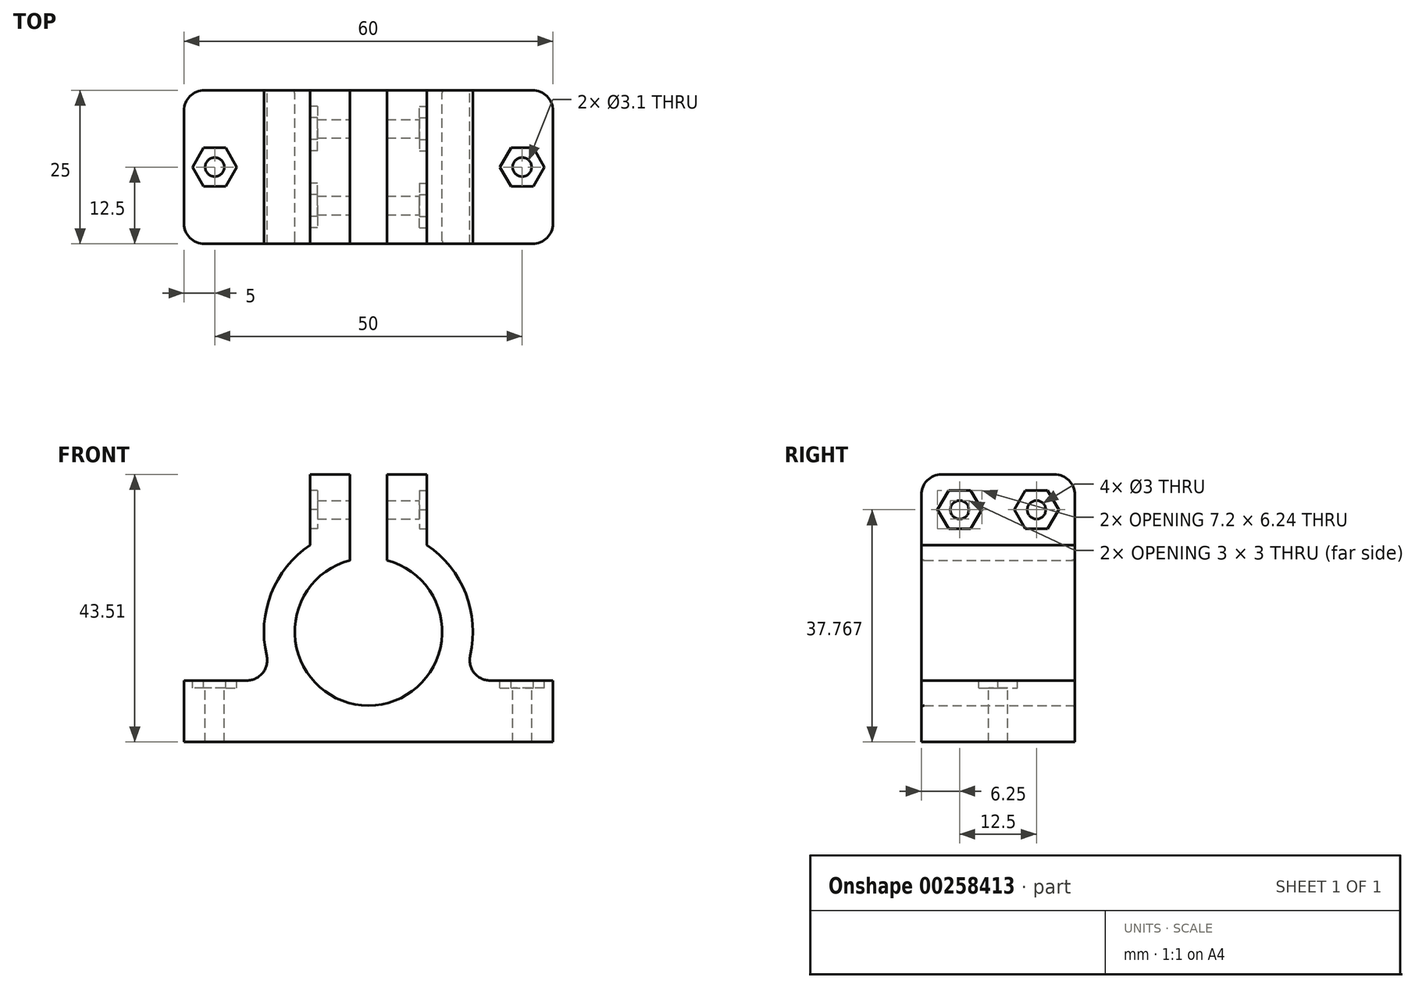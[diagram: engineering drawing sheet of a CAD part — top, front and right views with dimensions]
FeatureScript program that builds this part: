
annotation { "Feature Type Name" : "Feature", "Feature Type Description" : "" }
export const myFeature = defineFeature(function(context is Context, id is Id, definition is map)
    precondition{}
    {
        {
            var Q0;
            Q0=qCreatedBy(makeId("Front.planeOp"),FACE);
            var sketch = newSketch(context, id + "F0", { "sketchPlane" : qUnion([Q0])});
            skLineSegment(sketch, "E0.bottom", {"start": v(30, -29.77) * mm, "end": v(-30, -29.77) * mm});
            skLineSegment(sketch, "E0.left", {"start": v(30, -29.77) * mm, "end": v(30, -19.77) * mm});
            skLineSegment(sketch, "E0.right", {"start": v(-30, -29.77) * mm, "end": v(-30, -19.77) * mm});
            skPoint(sketch, "E0.middle", {"position": v(0, -24.77) * mm});
            skLineSegment(sketch, "E1", {"start": v(0, -29.77) * mm, "end": v(0, 6.08) * mm, "construction": true});
            skArc(sketch, "E2", {"start": v(-3, -0.23) * mm, "mid": v(0, -23.85) * mm, "end": v(3, -0.23) * mm});
            skArc(sketch, "E3.0", {"start": v(15.04, -19.77) * mm, "mid": v(16.49, -7.7) * mm, "end": v(9.5, 2.25) * mm});
            skLineSegment(sketch, "E4", {"start": v(-30, -19.77) * mm, "end": v(-15.04, -19.77) * mm});
            skLineSegment(sketch, "E5.MirrorCS", {"start": v(30, -19.77) * mm, "end": v(15.04, -19.77) * mm});
            skLineSegment(sketch, "E6.top", {"start": v(-9.5, 13.74) * mm, "end": v(-3, 13.74) * mm});
            skLineSegment(sketch, "E6.left", {"start": v(-9.5, 2.25) * mm, "end": v(-9.5, 13.74) * mm});
            skLineSegment(sketch, "E6.right", {"start": v(-3, 4.89) * mm, "end": v(-3, 13.74) * mm});
            skLineSegment(sketch, "E7.MirrorCS", {"start": v(3, 4.89) * mm, "end": v(3, 13.74) * mm});
            skLineSegment(sketch, "E8.MirrorCS", {"start": v(9.5, 2.25) * mm, "end": v(9.5, 13.74) * mm});
            skLineSegment(sketch, "E9.MirrorCS", {"start": v(9.5, 13.74) * mm, "end": v(3, 13.74) * mm});
            skArc(sketch, "E10.trimOffspring", {"start": v(-9.5, 2.25) * mm, "mid": v(-16.49, -7.7) * mm, "end": v(-15.04, -19.77) * mm});
            skPoint(sketch, "E11.orphan", {"position": v(-3, 2.25) * mm});
            skPoint(sketch, "E12.orphan", {"position": v(3, 2.25) * mm});
            skPoint(sketch, "E13.MirrorCS.start.orphan", {"position": v(9.5, 2.25) * mm});
            skLineSegment(sketch, "E14.left", {"start": v(-3, 4.89) * mm, "end": v(-3, -0.23) * mm});
            skLineSegment(sketch, "E14.right", {"start": v(3, 4.89) * mm, "end": v(3, -0.23) * mm});
            skSolve(sketch);
        }
        {
            var Q0;
            Q0=makeQuery(id+"F0.imprint","IMPRINT",FACE,{"disambiguationData":[TD([[makeQuery(id+"F0.imprint","IMPRINT",EDGE,{"derivedFrom":sQuery(id+"F0.wireOp",EDGE,"E0.bottom")}),-1.0]])]});
            extrude(context, id + "F1", {"entities" : qUnion([Q0]), "depth" : 25 * mm});
        }
        {
            var Q0;
            Q0=makeQuery(id+"F1.opExtrude","SWEPT_FACE",FACE,{"disambiguationData":[OSD([sQuery(id+"F0.wireOp",EDGE,"E4")])]});
            var sketch = newSketch(context, id + "F2", { "sketchPlane" : qUnion([Q0])});
            skLineSegment(sketch, "E15", {"start": v(-30, -12.5) * mm, "end": v(30, -12.5) * mm, "construction": true});
            skCircle(sketch, "E16", {"center": v(-25, -12.5) * mm, "radius": 1.55 * mm});
            skCircle(sketch, "E17.MirrorC", {"center": v(25, -12.5) * mm, "radius": 1.55 * mm});
            skSolve(sketch);
        }
        {
            var Q0;
            Q0=qSketchRegion(id+"F2",true);
            extrude(context, id + "F3", {"entities" : qUnion([Q0]), "operationType" : NewBodyOperationType.REMOVE, "oppositeDirection" : true, "depth" : 25 * mm});
        }
        {
            var Q0;
            Q0=makeQuery(id+"F1.opExtrude","SWEPT_FACE",FACE,{"disambiguationData":[OSD([sQuery(id+"F0.wireOp",EDGE,"E8.MirrorCS")])]});
            var sketch = newSketch(context, id + "F4", { "sketchPlane" : qUnion([Q0])});
            skLineSegment(sketch, "E18", {"start": v(-25, 8) * mm, "end": v(0, 8) * mm, "construction": true});
            skLineSegment(sketch, "E19", {"start": v(-12.5, 13.74) * mm, "end": v(-12.5, 2.25) * mm, "construction": true});
            skLineSegment(sketch, "E20", {"start": v(-18.75, 13.74) * mm, "end": v(-18.75, 2.25) * mm, "construction": true});
            skLineSegment(sketch, "E21.MirrorCS", {"start": v(-6.25, 13.74) * mm, "end": v(-6.25, 2.25) * mm, "construction": true});
            skCircle(sketch, "E22", {"center": v(-18.75, 8) * mm, "radius": 1.5 * mm});
            skCircle(sketch, "E23", {"center": v(-6.25, 8) * mm, "radius": 1.5 * mm});
            skSolve(sketch);
        }
        {
            var Q0;
            Q0=qSketchRegion(id+"F4",true);
            extrude(context, id + "F5", {"entities" : qUnion([Q0]), "operationType" : NewBodyOperationType.REMOVE, "oppositeDirection" : true, "depth" : 25 * mm});
        }
        {
            var Q0;
            Q0=makeQuery(id+"F1.opExtrude","CAP_EDGE",EDGE,{"disambiguationData":[OSD([sQuery(id+"F0.wireOp",EDGE,"E6.top")])],"isStart":false});
            var Q1;
            Q1=makeQuery(id+"F1.opExtrude","CAP_EDGE",EDGE,{"disambiguationData":[OSD([sQuery(id+"F0.wireOp",EDGE,"E9.MirrorCS")])],"isStart":false});
            var Q2;
            Q2=makeQuery(id+"F1.opExtrude","CAP_EDGE",EDGE,{"disambiguationData":[OSD([sQuery(id+"F0.wireOp",EDGE,"E6.top")])],"isStart":true});
            var Q3;
            Q3=makeQuery(id+"F1.opExtrude","CAP_EDGE",EDGE,{"disambiguationData":[OSD([sQuery(id+"F0.wireOp",EDGE,"E9.MirrorCS")])],"isStart":true});
            var Q4;
            Q4=makeQuery(id+"F1.opExtrude","CAP_EDGE",EDGE,{"disambiguationData":[OSD([sQuery(id+"F0.wireOp",EDGE,"E0.left")])],"isStart":false});
            var Q5;
            Q5=makeQuery(id+"F1.opExtrude","CAP_EDGE",EDGE,{"disambiguationData":[OSD([sQuery(id+"F0.wireOp",EDGE,"E0.left")])],"isStart":true});
            var Q6;
            Q6=makeQuery(id+"F1.opExtrude","CAP_EDGE",EDGE,{"disambiguationData":[OSD([sQuery(id+"F0.wireOp",EDGE,"E0.right")])],"isStart":true});
            var Q7;
            Q7=makeQuery(id+"F1.opExtrude","CAP_EDGE",EDGE,{"disambiguationData":[OSD([sQuery(id+"F0.wireOp",EDGE,"E0.right")])],"isStart":false});
            var Q8;
            Q8=makeQuery(id+"F1.opExtrude","SWEPT_EDGE",EDGE,{"disambiguationData":[OSD([sQuery(id+"F0.wireOp",EDGE,"E3.0"),sQuery(id+"F0.wireOp",EDGE,"E5.MirrorCS")])]});
            var Q9;
            Q9=makeQuery(id+"F1.opExtrude","SWEPT_EDGE",EDGE,{"disambiguationData":[OSD([sQuery(id+"F0.wireOp",EDGE,"E4"),sQuery(id+"F0.wireOp",EDGE,"E10.trimOffspring")])]});
            fillet(context, id + "F6", {"entities" : qUnion([Q0, Q1, Q2, Q3, Q4, Q5, Q6, Q7, Q8, Q9]), "radius" : 3.31 * mm, "tangentPropagation" : true, "allowEdgeOverflow" : false});
        }
        {
            var Q0;
            Q0=makeQuery(id+"F1.opExtrude","SWEPT_FACE",FACE,{"disambiguationData":[OSD([sQuery(id+"F0.wireOp",EDGE,"E8.MirrorCS")])]});
            var sketch = newSketch(context, id + "F7", { "sketchPlane" : qUnion([Q0])});
            skLineSegment(sketch, "E24", {"start": v(-12.5, 2.25) * mm, "end": v(-12.5, 13.74) * mm, "construction": true});
            skLineSegment(sketch, "E25", {"start": v(-12.5, 8) * mm, "end": v(-25, 8) * mm, "construction": true});
            skLineSegment(sketch, "E26", {"start": v(-12.5, 8) * mm, "end": v(0, 8) * mm, "construction": true});
            skCircle(sketch, "E27.cCircle", {"center": v(-18.75, 8) * mm, "radius": 3.12 * mm, "construction": true});
            skLineSegment(sketch, "E27.0", {"start": v(-16.95, 4.88) * mm, "end": v(-20.55, 4.88) * mm});
            skLineSegment(sketch, "E27.1", {"start": v(-20.55, 4.88) * mm, "end": v(-22.35, 8) * mm});
            skLineSegment(sketch, "E27.2", {"start": v(-22.35, 8) * mm, "end": v(-20.55, 11.11) * mm});
            skLineSegment(sketch, "E27.3", {"start": v(-20.55, 11.11) * mm, "end": v(-16.95, 11.11) * mm});
            skLineSegment(sketch, "E27.4", {"start": v(-16.95, 11.11) * mm, "end": v(-15.15, 8) * mm});
            skLineSegment(sketch, "E27.5", {"start": v(-15.15, 8) * mm, "end": v(-16.95, 4.88) * mm});
            skPoint(sketch, "E27.0.midPoint", {"position": v(-18.75, 4.88) * mm});
            skLineSegment(sketch, "E28.MirrorCS", {"start": v(-8.05, 11.11) * mm, "end": v(-9.85, 8) * mm});
            skLineSegment(sketch, "E29.MirrorCS", {"start": v(-4.45, 11.11) * mm, "end": v(-8.05, 11.11) * mm});
            skLineSegment(sketch, "E30.MirrorCS", {"start": v(-2.65, 8) * mm, "end": v(-4.45, 11.11) * mm});
            skLineSegment(sketch, "E31.MirrorCS", {"start": v(-4.45, 4.88) * mm, "end": v(-2.65, 8) * mm});
            skLineSegment(sketch, "E32.MirrorCS", {"start": v(-8.05, 4.88) * mm, "end": v(-4.45, 4.88) * mm});
            skLineSegment(sketch, "E33.MirrorCS", {"start": v(-9.85, 8) * mm, "end": v(-8.05, 4.88) * mm});
            skSolve(sketch);
        }
        {
            var Q0;
            Q0=makeQuery(id+"F1.opExtrude","SWEPT_FACE",FACE,{"disambiguationData":[OSD([sQuery(id+"F0.wireOp",EDGE,"E6.left")])]});
            var sketch = newSketch(context, id + "F8", { "sketchPlane" : qUnion([Q0])});
            skLineSegment(sketch, "E34", {"start": v(12.5, 13.74) * mm, "end": v(12.5, 2.25) * mm, "construction": true});
            skLineSegment(sketch, "E35", {"start": v(12.5, 8) * mm, "end": v(0, 8) * mm, "construction": true});
            skLineSegment(sketch, "E36", {"start": v(12.5, 8) * mm, "end": v(25, 8) * mm, "construction": true});
            skCircle(sketch, "E37.cCircle", {"center": v(6.25, 8) * mm, "radius": 3.12 * mm, "construction": true});
            skLineSegment(sketch, "E37.0", {"start": v(8.05, 4.88) * mm, "end": v(4.45, 4.88) * mm});
            skLineSegment(sketch, "E37.1", {"start": v(4.45, 4.88) * mm, "end": v(2.65, 8) * mm});
            skLineSegment(sketch, "E37.2", {"start": v(2.65, 8) * mm, "end": v(4.45, 11.11) * mm});
            skLineSegment(sketch, "E37.3", {"start": v(4.45, 11.11) * mm, "end": v(8.05, 11.11) * mm});
            skLineSegment(sketch, "E37.4", {"start": v(8.05, 11.11) * mm, "end": v(9.85, 8) * mm});
            skLineSegment(sketch, "E37.5", {"start": v(9.85, 8) * mm, "end": v(8.05, 4.88) * mm});
            skPoint(sketch, "E37.0.midPoint", {"position": v(6.25, 4.88) * mm});
            skLineSegment(sketch, "E38.MirrorCS", {"start": v(16.95, 11.11) * mm, "end": v(15.15, 8) * mm});
            skLineSegment(sketch, "E39.MirrorCS", {"start": v(20.55, 11.11) * mm, "end": v(16.95, 11.11) * mm});
            skLineSegment(sketch, "E40.MirrorCS", {"start": v(22.35, 8) * mm, "end": v(20.55, 11.11) * mm});
            skLineSegment(sketch, "E41.MirrorCS", {"start": v(20.55, 4.88) * mm, "end": v(22.35, 8) * mm});
            skLineSegment(sketch, "E42.MirrorCS", {"start": v(16.95, 4.88) * mm, "end": v(20.55, 4.88) * mm});
            skLineSegment(sketch, "E43.MirrorCS", {"start": v(15.15, 8) * mm, "end": v(16.95, 4.88) * mm});
            skSolve(sketch);
        }
        {
            var Q0;
            Q0 = qSketchRegion(id + "F7", true);
            extrude(context, id + "F9", {"entities" : qUnion([Q0]), "operationType" : NewBodyOperationType.REMOVE, "oppositeDirection" : true, "depth" : 1.2 * mm});
        }
        {
            var Q0;
            Q0=makeQuery(id+"F8.imprint","IMPRINT",FACE,{"disambiguationData":[TD([[makeQuery(id+"F8.imprint","IMPRINT",EDGE,{"derivedFrom":sQuery(id+"F8.wireOp",EDGE,"E37.0")}),-1.0]])]});
            var Q1;
            Q1=makeQuery(id+"F8.imprint","IMPRINT",FACE,{"disambiguationData":[TD([[makeQuery(id+"F8.imprint","IMPRINT",EDGE,{"derivedFrom":sQuery(id+"F8.wireOp",EDGE,"E38.MirrorCS")}),1.0]])]});
            extrude(context, id + "F10", {"entities" : qUnion([Q0, Q1]), "operationType" : NewBodyOperationType.REMOVE, "oppositeDirection" : true, "depth" : 1.2 * mm});
        }
        {
            var Q0;
            Q0=makeQuery(id+"F1.opExtrude","SWEPT_FACE",FACE,{"disambiguationData":[OSD([sQuery(id+"F0.wireOp",EDGE,"E5.MirrorCS")])]});
            var sketch = newSketch(context, id + "F11", { "sketchPlane" : qUnion([Q0])});
            skLineSegment(sketch, "E44", {"start": v(30, -12.5) * mm, "end": v(-33.17, -12.5) * mm, "construction": true});
            skCircle(sketch, "E45.cCircle", {"center": v(25, -12.5) * mm, "radius": 3.12 * mm, "construction": true});
            skLineSegment(sketch, "E45.0", {"start": v(23.2, -9.38) * mm, "end": v(26.8, -9.38) * mm});
            skLineSegment(sketch, "E45.1", {"start": v(26.8, -9.38) * mm, "end": v(28.6, -12.5) * mm});
            skLineSegment(sketch, "E45.2", {"start": v(28.6, -12.5) * mm, "end": v(26.8, -15.62) * mm});
            skLineSegment(sketch, "E45.3", {"start": v(26.8, -15.62) * mm, "end": v(23.2, -15.62) * mm});
            skLineSegment(sketch, "E45.4", {"start": v(23.2, -15.62) * mm, "end": v(21.4, -12.5) * mm});
            skLineSegment(sketch, "E45.5", {"start": v(21.4, -12.5) * mm, "end": v(23.2, -9.38) * mm});
            skPoint(sketch, "E45.0.midPoint", {"position": v(25, -9.38) * mm});
            skLineSegment(sketch, "E46", {"start": v(0, -31.39) * mm, "end": v(0, 22.98) * mm, "construction": true});
            skLineSegment(sketch, "E47.MirrorCS", {"start": v(-21.4, -12.5) * mm, "end": v(-23.2, -9.38) * mm});
            skLineSegment(sketch, "E48.MirrorCS", {"start": v(-23.2, -15.62) * mm, "end": v(-21.4, -12.5) * mm});
            skLineSegment(sketch, "E49.MirrorCS", {"start": v(-26.8, -15.62) * mm, "end": v(-23.2, -15.62) * mm});
            skLineSegment(sketch, "E50.MirrorCS", {"start": v(-28.6, -12.5) * mm, "end": v(-26.8, -15.62) * mm});
            skLineSegment(sketch, "E51.MirrorCS", {"start": v(-26.8, -9.38) * mm, "end": v(-28.6, -12.5) * mm});
            skLineSegment(sketch, "E52.MirrorCS", {"start": v(-23.2, -9.38) * mm, "end": v(-26.8, -9.38) * mm});
            skSolve(sketch);
        }
        {
            var Q0;
            Q0 = qSketchRegion(id + "F11", true);
            extrude(context, id + "F12", {"entities" : qUnion([Q0]), "operationType" : NewBodyOperationType.REMOVE, "oppositeDirection" : true, "depth" : 1.2 * mm});
        }
        {
            var Q0;
            Q0=makeQuery(id+"F1.opExtrude","CAP_EDGE",EDGE,{"disambiguationData":[OSD([sQuery(id+"F0.wireOp",EDGE,"E2")])],"isStart":true});
            var Q1;
            Q1=makeQuery(id+"F1.opExtrude","CAP_EDGE",EDGE,{"disambiguationData":[OSD([sQuery(id+"F0.wireOp",EDGE,"E2")])],"isStart":false});
            fillet(context, id + "F13", {"entities" : qUnion([Q0, Q1]), "radius" : .5 * mm, "tangentPropagation" : true, "allowEdgeOverflow" : false});
        }
    });
